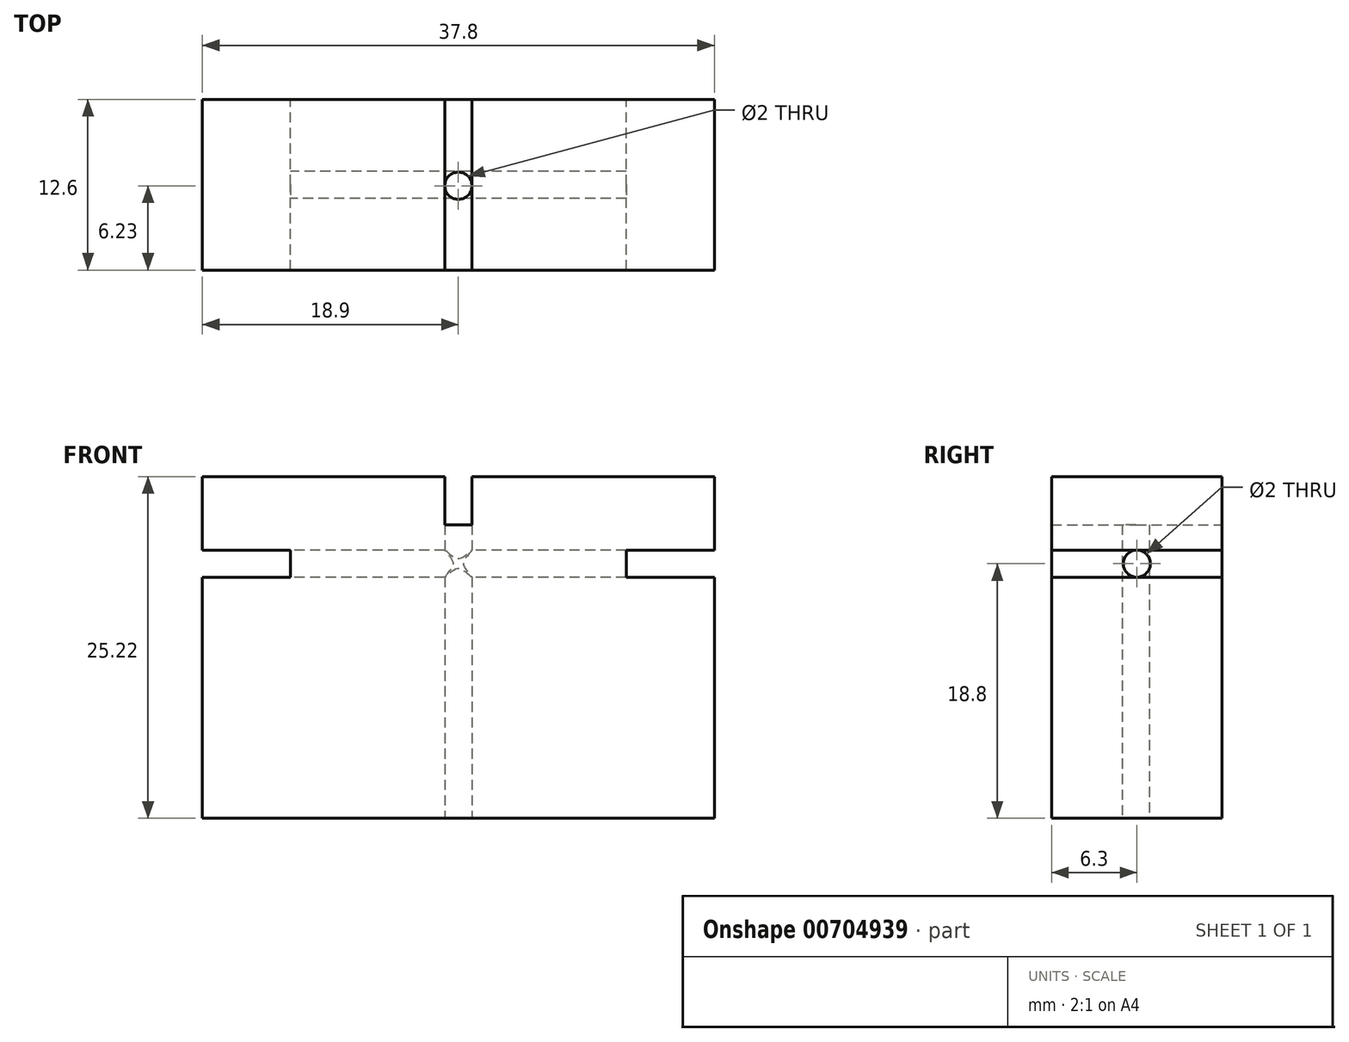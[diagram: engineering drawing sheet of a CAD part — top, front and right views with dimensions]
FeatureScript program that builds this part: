
annotation { "Feature Type Name" : "Feature", "Feature Type Description" : "" }
export const myFeature = defineFeature(function(context is Context, id is Id, definition is map)
    precondition{}
    {
        {
            var Q0;
            Q0=qCreatedBy(makeId("Front.planeOp"),FACE);
            var sketch = newSketch(context, id + "F0", { "sketchPlane" : qUnion([Q0])});
            skLineSegment(sketch, "E0.bottom", {"start": v(-18.9, 12.6) * mm, "end": v(-1, 12.6) * mm});
            skLineSegment(sketch, "E0.top", {"start": v(-18.9, -12.6) * mm, "end": v(18.9, -12.61) * mm});
            skLineSegment(sketch, "E0.left", {"start": v(-18.9, 12.6) * mm, "end": v(-18.9, 7.19) * mm});
            skLineSegment(sketch, "E0.right", {"start": v(18.9, 12.6) * mm, "end": v(18.9, 7.19) * mm});
            skPoint(sketch, "E0.middle", {"position": v(0, 0) * mm});
            skLineSegment(sketch, "E1", {"start": v(-1, 12.6) * mm, "end": v(-1, 9.06) * mm});
            skLineSegment(sketch, "E2", {"start": v(-1, 9.06) * mm, "end": v(0, 9.06) * mm});
            skLineSegment(sketch, "E3.MirrorCS", {"start": v(1, 12.6) * mm, "end": v(1, 9.06) * mm});
            skLineSegment(sketch, "E4.MirrorCS", {"start": v(1, 9.06) * mm, "end": v(0, 9.06) * mm});
            skLineSegment(sketch, "E5.trimOffspring", {"start": v(1, 12.6) * mm, "end": v(18.9, 12.61) * mm});
            skLineSegment(sketch, "E6", {"start": v(18.9, 7.2) * mm, "end": v(12.4, 7.2) * mm});
            skLineSegment(sketch, "E7", {"start": v(12.4, 7.2) * mm, "end": v(12.4, 5.2) * mm});
            skLineSegment(sketch, "E8", {"start": v(12.4, 5.2) * mm, "end": v(18.9, 5.2) * mm});
            skLineSegment(sketch, "E9.trimOffspring", {"start": v(18.9, 5.2) * mm, "end": v(18.9, -12.6) * mm});
            skLineSegment(sketch, "E10.MirrorCS", {"start": v(-18.9, 7.19) * mm, "end": v(-12.4, 7.19) * mm});
            skLineSegment(sketch, "E11.MirrorCS", {"start": v(-12.4, 7.2) * mm, "end": v(-12.4, 5.2) * mm});
            skLineSegment(sketch, "E12.MirrorCS", {"start": v(-12.4, 5.2) * mm, "end": v(-18.9, 5.2) * mm});
            skLineSegment(sketch, "E13.trimOffspring", {"start": v(-18.9, 5.2) * mm, "end": v(-18.9, -12.6) * mm});
            skSolve(sketch);
        }
        {
            var Q0;
            Q0 = qSketchRegion(id + "F0", true);
            extrude(context, id + "F1", {"entities" : qUnion([Q0]), "depth" : 12.6 * mm, "offsetDistance" : 25 * mm});
        }
        {
            var Q0;
            Q0=makeQuery(id+"F1.opExtrude","SWEPT_FACE",FACE,{"disambiguationData":[OSD([sQuery(id+"F0.wireOp",EDGE,"E0.top")])]});
            var sketch = newSketch(context, id + "F2", { "sketchPlane" : qUnion([Q0])});
            skLineSegment(sketch, "E14", {"start": v(0, 16.78) * mm, "end": v(0, -2.54) * mm, "construction": true});
            skLineSegment(sketch, "E15", {"start": v(-24.28, 6.37) * mm, "end": v(24.24, 6.37) * mm, "construction": true});
            skPoint(sketch, "E16", {"position": v(0, 6.37) * mm});
            skCircle(sketch, "E17", {"center": v(0, 6.37) * mm, "radius": 1 * mm});
            skSolve(sketch);
        }
        {
            var Q0;
            Q0=makeQuery(id+"F2.imprint","IMPRINT",FACE,{"disambiguationData":[TD([[makeQuery(id+"F2.imprint","IMPRINT",EDGE,{"derivedFrom":sQuery(id+"F2.wireOp",EDGE,"E17")}),1.0]])]});
            var Q1;
            Q1=makeQuery(id+"F2.imprint","IMPRINT",FACE,{"disambiguationData":[TD([[makeQuery(id+"F2.imprint","IMPRINT",EDGE,{"derivedFrom":sQuery(id+"F2.wireOp",EDGE,"01632166-f06f-4588-bbc3-6d80b79cbc2d0.MirrorC")}),-1.0]])]});
            var Q2;
            Q2=makeQuery(id+"F2.imprint","IMPRINT",FACE,{"disambiguationData":[TD([[makeQuery(id+"F2.imprint","IMPRINT",EDGE,{"derivedFrom":sQuery(id+"F2.wireOp",EDGE,"spDxz6Rt-2bDh-TdtU-N9AU-h3lXGEMHulBt")}),1.0]])]});
            var Q3;
            Q3=sQuery(id+"F2.wireOp",EDGE,"E17");
            extrude(context, id + "F3", {"entities" : qUnion([Q0, Q1, Q2]), "operationType" : NewBodyOperationType.REMOVE, "surfaceEntities" : qUnion([Q3]), "oppositeDirection" : true, "depth" : 22 * mm, "offsetDistance" : 25 * mm});
        }
        {
            var Q0;
            Q0=makeQuery(id+"F1.opExtrude","SWEPT_FACE",FACE,{"disambiguationData":[OSD([sQuery(id+"F0.wireOp",EDGE,"E11.MirrorCS")])]});
            var sketch = newSketch(context, id + "F4", { "sketchPlane" : qUnion([Q0])});
            skPoint(sketch, "E18", {"position": v(6.3, 6.2) * mm});
            skPoint(sketch, "E18.positionSnap0", {"position": v(6.3, 5.2) * mm});
            skCircle(sketch, "E19", {"center": v(6.3, 6.2) * mm, "radius": 1 * mm});
            skSolve(sketch);
        }
        {
            var Q0;
            {var subQ0=sQuery(id+"F4.wireOp",EDGE,"E19");var subQ1=sQuery(id+"F0.wireOp",EDGE,"E11.MirrorCS");var subQ2=makeQuery(id+"F4.imprint","INTERSECT",VERTEX,{"derivedFrom":[makeQuery(id+"F1.opExtrude","SWEPT_EDGE",EDGE,{"disambiguationData":[OSD([sQuery(id+"F0.wireOp",EDGE,"E10.MirrorCS"),subQ1])]}),subQ0]});Q0=makeQuery(id+"F4.imprint","IMPRINT",FACE,{"disambiguationData":[TD([[makeQuery(id+"F4.imprint","IMPRINT",EDGE,{"disambiguationData":[TD([[subQ2,-1.0]])],"derivedFrom":subQ0}),1.0]])]});}
            extrude(context, id + "F5", {"entities" : qUnion([Q0]), "operationType" : NewBodyOperationType.REMOVE, "endBound" : BoundingType.THROUGH_ALL, "oppositeDirection" : true, "depth" : 25 * mm, "offsetDistance" : 25 * mm});
        }
    });
